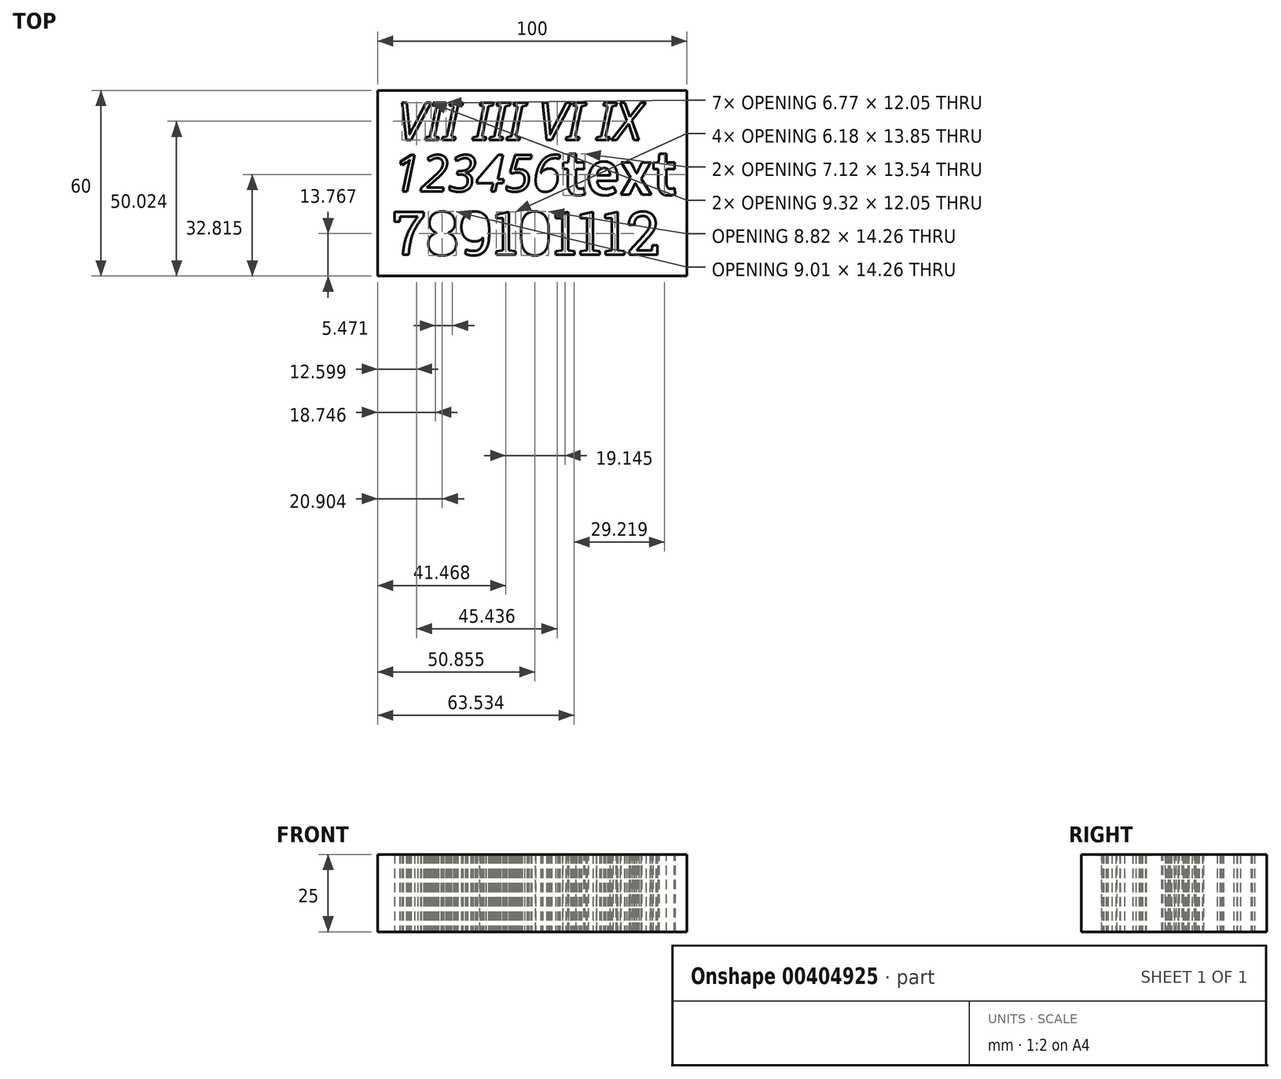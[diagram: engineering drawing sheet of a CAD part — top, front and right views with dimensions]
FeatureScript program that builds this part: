
annotation { "Feature Type Name" : "Feature", "Feature Type Description" : "" }
export const myFeature = defineFeature(function(context is Context, id is Id, definition is map)
    precondition{}
    {
        {
            var Q0;
            Q0=qCreatedBy(makeId("Top.planeOp"),FACE);
            var sketch = newSketch(context, id + "F0", { "sketchPlane" : qUnion([Q0])});
            skText(sketch, "E0", { "text": "VII III VI IX", "fontName": "NotoSans-Italic.ttf"});
            skText(sketch, "E1", { "text": "123456", "fontName": "OpenSans-Italic.ttf"});
            skText(sketch, "E2", { "text": "789101112", "fontName": "RobotoSlab-Regular.ttf"});
            skLineSegment(sketch, "E3.bottom", {"start": v(-47.92, 39.13) * mm, "end": v(52.08, 39.13) * mm});
            skLineSegment(sketch, "E3.top", {"start": v(-47.92, -20.87) * mm, "end": v(52.08, -20.87) * mm});
            skLineSegment(sketch, "E3.left", {"start": v(-47.92, 39.13) * mm, "end": v(-47.92, -20.87) * mm});
            skLineSegment(sketch, "E3.right", {"start": v(52.08, 39.13) * mm, "end": v(52.08, -20.87) * mm});
            const initialGuessF0  = {"E0": [-0.04153, 0.02313, 1, 0, 0.01215], "E1": [-0.04313, 0.0065, 1, 0, 0.01183], "E2": [-0.04313, -0.01403, 1, 0, 0.01403]};
            skSetInitialGuess(sketch, initialGuessF0);
            skSolve(sketch);
        }
        {
            var Q0;
            Q0 = qSketchRegion(id + "F0", true);
            extrude(context, id + "F1", {"entities" : qUnion([Q0]), "depth" : 25 * mm});
        }
        {
            var Q0;
            Q0=makeQuery(id+"F1.opExtrude","CAP_FACE",FACE,{"disambiguationData":[OSD([sQuery(id+"F0.wireOp",EDGE,"E0.sketch_text.stroke-0"),sQuery(id+"F0.wireOp",EDGE,"E0.sketch_text.stroke-1"),sQuery(id+"F0.wireOp",EDGE,"E0.sketch_text.stroke-2"),sQuery(id+"F0.wireOp",EDGE,"E0.sketch_text.stroke-3"),sQuery(id+"F0.wireOp",EDGE,"E0.sketch_text.stroke-4"),sQuery(id+"F0.wireOp",EDGE,"E0.sketch_text.stroke-5"),sQuery(id+"F0.wireOp",EDGE,"E0.sketch_text.stroke-6"),sQuery(id+"F0.wireOp",EDGE,"E0.sketch_text.stroke-7"),sQuery(id+"F0.wireOp",EDGE,"E0.sketch_text.stroke-8"),sQuery(id+"F0.wireOp",EDGE,"E0.sketch_text.stroke-9"),sQuery(id+"F0.wireOp",EDGE,"E0.sketch_text.stroke-10"),sQuery(id+"F0.wireOp",EDGE,"E0.sketch_text.stroke-11"),sQuery(id+"F0.wireOp",EDGE,"E0.sketch_text.stroke-12"),sQuery(id+"F0.wireOp",EDGE,"E0.sketch_text.stroke-13"),sQuery(id+"F0.wireOp",EDGE,"E0.sketch_text.stroke-14"),sQuery(id+"F0.wireOp",EDGE,"E0.sketch_text.stroke-15"),sQuery(id+"F0.wireOp",EDGE,"E0.sketch_text.stroke-16"),sQuery(id+"F0.wireOp",EDGE,"E0.sketch_text.stroke-17"),sQuery(id+"F0.wireOp",EDGE,"E0.sketch_text.stroke-18"),sQuery(id+"F0.wireOp",EDGE,"E0.sketch_text.stroke-19"),sQuery(id+"F0.wireOp",EDGE,"E0.sketch_text.stroke-20"),sQuery(id+"F0.wireOp",EDGE,"E0.sketch_text.stroke-21"),sQuery(id+"F0.wireOp",EDGE,"E0.sketch_text.stroke-22"),sQuery(id+"F0.wireOp",EDGE,"E0.sketch_text.stroke-23"),sQuery(id+"F0.wireOp",EDGE,"E0.sketch_text.stroke-24"),sQuery(id+"F0.wireOp",EDGE,"E0.sketch_text.stroke-25"),sQuery(id+"F0.wireOp",EDGE,"E0.sketch_text.stroke-26"),sQuery(id+"F0.wireOp",EDGE,"E0.sketch_text.stroke-27"),sQuery(id+"F0.wireOp",EDGE,"E0.sketch_text.stroke-28"),sQuery(id+"F0.wireOp",EDGE,"E0.sketch_text.stroke-29"),sQuery(id+"F0.wireOp",EDGE,"E0.sketch_text.stroke-30"),sQuery(id+"F0.wireOp",EDGE,"E0.sketch_text.stroke-31"),sQuery(id+"F0.wireOp",EDGE,"E0.sketch_text.stroke-32"),sQuery(id+"F0.wireOp",EDGE,"E0.sketch_text.stroke-33"),sQuery(id+"F0.wireOp",EDGE,"E0.sketch_text.stroke-34"),sQuery(id+"F0.wireOp",EDGE,"E0.sketch_text.stroke-35"),sQuery(id+"F0.wireOp",EDGE,"E0.sketch_text.stroke-36"),sQuery(id+"F0.wireOp",EDGE,"E0.sketch_text.stroke-37"),sQuery(id+"F0.wireOp",EDGE,"E0.sketch_text.stroke-38"),sQuery(id+"F0.wireOp",EDGE,"E0.sketch_text.stroke-39"),sQuery(id+"F0.wireOp",EDGE,"E0.sketch_text.stroke-40"),sQuery(id+"F0.wireOp",EDGE,"E0.sketch_text.stroke-41"),sQuery(id+"F0.wireOp",EDGE,"E0.sketch_text.stroke-42"),sQuery(id+"F0.wireOp",EDGE,"E0.sketch_text.stroke-43"),sQuery(id+"F0.wireOp",EDGE,"E0.sketch_text.stroke-44"),sQuery(id+"F0.wireOp",EDGE,"E0.sketch_text.stroke-45"),sQuery(id+"F0.wireOp",EDGE,"E0.sketch_text.stroke-46"),sQuery(id+"F0.wireOp",EDGE,"E0.sketch_text.stroke-47"),sQuery(id+"F0.wireOp",EDGE,"E0.sketch_text.stroke-48"),sQuery(id+"F0.wireOp",EDGE,"E0.sketch_text.stroke-49"),sQuery(id+"F0.wireOp",EDGE,"E0.sketch_text.stroke-50"),sQuery(id+"F0.wireOp",EDGE,"E0.sketch_text.stroke-51"),sQuery(id+"F0.wireOp",EDGE,"E0.sketch_text.stroke-52"),sQuery(id+"F0.wireOp",EDGE,"E0.sketch_text.stroke-53"),sQuery(id+"F0.wireOp",EDGE,"E0.sketch_text.stroke-54"),sQuery(id+"F0.wireOp",EDGE,"E0.sketch_text.stroke-55"),sQuery(id+"F0.wireOp",EDGE,"E0.sketch_text.stroke-56"),sQuery(id+"F0.wireOp",EDGE,"E0.sketch_text.stroke-57"),sQuery(id+"F0.wireOp",EDGE,"E0.sketch_text.stroke-58"),sQuery(id+"F0.wireOp",EDGE,"E0.sketch_text.stroke-59"),sQuery(id+"F0.wireOp",EDGE,"E0.sketch_text.stroke-60"),sQuery(id+"F0.wireOp",EDGE,"E0.sketch_text.stroke-61"),sQuery(id+"F0.wireOp",EDGE,"E0.sketch_text.stroke-62"),sQuery(id+"F0.wireOp",EDGE,"E0.sketch_text.stroke-63"),sQuery(id+"F0.wireOp",EDGE,"E0.sketch_text.stroke-64"),sQuery(id+"F0.wireOp",EDGE,"E0.sketch_text.stroke-65"),sQuery(id+"F0.wireOp",EDGE,"E0.sketch_text.stroke-66"),sQuery(id+"F0.wireOp",EDGE,"E0.sketch_text.stroke-67"),sQuery(id+"F0.wireOp",EDGE,"E0.sketch_text.stroke-68"),sQuery(id+"F0.wireOp",EDGE,"E0.sketch_text.stroke-69"),sQuery(id+"F0.wireOp",EDGE,"E0.sketch_text.stroke-70"),sQuery(id+"F0.wireOp",EDGE,"E0.sketch_text.stroke-71"),sQuery(id+"F0.wireOp",EDGE,"E0.sketch_text.stroke-72"),sQuery(id+"F0.wireOp",EDGE,"E0.sketch_text.stroke-73"),sQuery(id+"F0.wireOp",EDGE,"E0.sketch_text.stroke-74"),sQuery(id+"F0.wireOp",EDGE,"E0.sketch_text.stroke-75"),sQuery(id+"F0.wireOp",EDGE,"E0.sketch_text.stroke-76"),sQuery(id+"F0.wireOp",EDGE,"E0.sketch_text.stroke-77"),sQuery(id+"F0.wireOp",EDGE,"E0.sketch_text.stroke-78"),sQuery(id+"F0.wireOp",EDGE,"E0.sketch_text.stroke-79"),sQuery(id+"F0.wireOp",EDGE,"E0.sketch_text.stroke-80"),sQuery(id+"F0.wireOp",EDGE,"E0.sketch_text.stroke-81"),sQuery(id+"F0.wireOp",EDGE,"E0.sketch_text.stroke-82"),sQuery(id+"F0.wireOp",EDGE,"E0.sketch_text.stroke-83"),sQuery(id+"F0.wireOp",EDGE,"E0.sketch_text.stroke-84"),sQuery(id+"F0.wireOp",EDGE,"E0.sketch_text.stroke-85"),sQuery(id+"F0.wireOp",EDGE,"E0.sketch_text.stroke-86"),sQuery(id+"F0.wireOp",EDGE,"E0.sketch_text.stroke-87"),sQuery(id+"F0.wireOp",EDGE,"E0.sketch_text.stroke-88"),sQuery(id+"F0.wireOp",EDGE,"E0.sketch_text.stroke-89"),sQuery(id+"F0.wireOp",EDGE,"E0.sketch_text.stroke-90"),sQuery(id+"F0.wireOp",EDGE,"E0.sketch_text.stroke-91"),sQuery(id+"F0.wireOp",EDGE,"E0.sketch_text.stroke-92"),sQuery(id+"F0.wireOp",EDGE,"E0.sketch_text.stroke-93"),sQuery(id+"F0.wireOp",EDGE,"E0.sketch_text.stroke-94"),sQuery(id+"F0.wireOp",EDGE,"E0.sketch_text.stroke-95"),sQuery(id+"F0.wireOp",EDGE,"E0.sketch_text.stroke-96"),sQuery(id+"F0.wireOp",EDGE,"E0.sketch_text.stroke-97"),sQuery(id+"F0.wireOp",EDGE,"E0.sketch_text.stroke-98"),sQuery(id+"F0.wireOp",EDGE,"E0.sketch_text.stroke-99"),sQuery(id+"F0.wireOp",EDGE,"E0.sketch_text.stroke-100"),sQuery(id+"F0.wireOp",EDGE,"E0.sketch_text.stroke-101"),sQuery(id+"F0.wireOp",EDGE,"E0.sketch_text.stroke-102"),sQuery(id+"F0.wireOp",EDGE,"E0.sketch_text.stroke-103"),sQuery(id+"F0.wireOp",EDGE,"E0.sketch_text.stroke-104"),sQuery(id+"F0.wireOp",EDGE,"E0.sketch_text.stroke-105"),sQuery(id+"F0.wireOp",EDGE,"E0.sketch_text.stroke-106"),sQuery(id+"F0.wireOp",EDGE,"E0.sketch_text.stroke-107"),sQuery(id+"F0.wireOp",EDGE,"E0.sketch_text.stroke-108"),sQuery(id+"F0.wireOp",EDGE,"E0.sketch_text.stroke-109"),sQuery(id+"F0.wireOp",EDGE,"E0.sketch_text.stroke-110"),sQuery(id+"F0.wireOp",EDGE,"E0.sketch_text.stroke-111"),sQuery(id+"F0.wireOp",EDGE,"E0.sketch_text.stroke-112"),sQuery(id+"F0.wireOp",EDGE,"E0.sketch_text.stroke-113"),sQuery(id+"F0.wireOp",EDGE,"E0.sketch_text.stroke-114"),sQuery(id+"F0.wireOp",EDGE,"E0.sketch_text.stroke-115"),sQuery(id+"F0.wireOp",EDGE,"E0.sketch_text.stroke-116"),sQuery(id+"F0.wireOp",EDGE,"E0.sketch_text.stroke-117"),sQuery(id+"F0.wireOp",EDGE,"E1.sketch_text.stroke-0"),sQuery(id+"F0.wireOp",EDGE,"E1.sketch_text.stroke-1"),sQuery(id+"F0.wireOp",EDGE,"E1.sketch_text.stroke-2"),sQuery(id+"F0.wireOp",EDGE,"E1.sketch_text.stroke-3"),sQuery(id+"F0.wireOp",EDGE,"E1.sketch_text.stroke-4"),sQuery(id+"F0.wireOp",EDGE,"E1.sketch_text.stroke-5"),sQuery(id+"F0.wireOp",EDGE,"E1.sketch_text.stroke-6"),sQuery(id+"F0.wireOp",EDGE,"E1.sketch_text.stroke-7"),sQuery(id+"F0.wireOp",EDGE,"E1.sketch_text.stroke-8"),sQuery(id+"F0.wireOp",EDGE,"E1.sketch_text.stroke-9"),sQuery(id+"F0.wireOp",EDGE,"E1.sketch_text.stroke-10"),sQuery(id+"F0.wireOp",EDGE,"E1.sketch_text.stroke-11"),sQuery(id+"F0.wireOp",EDGE,"E1.sketch_text.stroke-12"),sQuery(id+"F0.wireOp",EDGE,"E1.sketch_text.stroke-13"),sQuery(id+"F0.wireOp",EDGE,"E1.sketch_text.stroke-14"),sQuery(id+"F0.wireOp",EDGE,"E1.sketch_text.stroke-15"),sQuery(id+"F0.wireOp",EDGE,"E1.sketch_text.stroke-16"),sQuery(id+"F0.wireOp",EDGE,"E1.sketch_text.stroke-17"),sQuery(id+"F0.wireOp",EDGE,"E1.sketch_text.stroke-18"),sQuery(id+"F0.wireOp",EDGE,"E1.sketch_text.stroke-19"),sQuery(id+"F0.wireOp",EDGE,"E1.sketch_text.stroke-20"),sQuery(id+"F0.wireOp",EDGE,"E1.sketch_text.stroke-21"),sQuery(id+"F0.wireOp",EDGE,"E1.sketch_text.stroke-22"),sQuery(id+"F0.wireOp",EDGE,"E1.sketch_text.stroke-23"),sQuery(id+"F0.wireOp",EDGE,"E1.sketch_text.stroke-24"),sQuery(id+"F0.wireOp",EDGE,"E1.sketch_text.stroke-25"),sQuery(id+"F0.wireOp",EDGE,"E1.sketch_text.stroke-26"),sQuery(id+"F0.wireOp",EDGE,"E1.sketch_text.stroke-27"),sQuery(id+"F0.wireOp",EDGE,"E1.sketch_text.stroke-28"),sQuery(id+"F0.wireOp",EDGE,"E1.sketch_text.stroke-29"),sQuery(id+"F0.wireOp",EDGE,"E1.sketch_text.stroke-30"),sQuery(id+"F0.wireOp",EDGE,"E1.sketch_text.stroke-31"),sQuery(id+"F0.wireOp",EDGE,"E1.sketch_text.stroke-32"),sQuery(id+"F0.wireOp",EDGE,"E1.sketch_text.stroke-33"),sQuery(id+"F0.wireOp",EDGE,"E1.sketch_text.stroke-34"),sQuery(id+"F0.wireOp",EDGE,"E1.sketch_text.stroke-35"),sQuery(id+"F0.wireOp",EDGE,"E1.sketch_text.stroke-36"),sQuery(id+"F0.wireOp",EDGE,"E1.sketch_text.stroke-37"),sQuery(id+"F0.wireOp",EDGE,"E1.sketch_text.stroke-38"),sQuery(id+"F0.wireOp",EDGE,"E1.sketch_text.stroke-39"),sQuery(id+"F0.wireOp",EDGE,"E1.sketch_text.stroke-40"),sQuery(id+"F0.wireOp",EDGE,"E1.sketch_text.stroke-41"),sQuery(id+"F0.wireOp",EDGE,"E1.sketch_text.stroke-42"),sQuery(id+"F0.wireOp",EDGE,"E1.sketch_text.stroke-43"),sQuery(id+"F0.wireOp",EDGE,"E1.sketch_text.stroke-44"),sQuery(id+"F0.wireOp",EDGE,"E1.sketch_text.stroke-45"),sQuery(id+"F0.wireOp",EDGE,"E1.sketch_text.stroke-46"),sQuery(id+"F0.wireOp",EDGE,"E1.sketch_text.stroke-47"),sQuery(id+"F0.wireOp",EDGE,"E1.sketch_text.stroke-48"),sQuery(id+"F0.wireOp",EDGE,"E1.sketch_text.stroke-49"),sQuery(id+"F0.wireOp",EDGE,"E1.sketch_text.stroke-50"),sQuery(id+"F0.wireOp",EDGE,"E1.sketch_text.stroke-51"),sQuery(id+"F0.wireOp",EDGE,"E1.sketch_text.stroke-52"),sQuery(id+"F0.wireOp",EDGE,"E1.sketch_text.stroke-53"),sQuery(id+"F0.wireOp",EDGE,"E1.sketch_text.stroke-54"),sQuery(id+"F0.wireOp",EDGE,"E1.sketch_text.stroke-55"),sQuery(id+"F0.wireOp",EDGE,"E1.sketch_text.stroke-56"),sQuery(id+"F0.wireOp",EDGE,"E1.sketch_text.stroke-57"),sQuery(id+"F0.wireOp",EDGE,"E1.sketch_text.stroke-58"),sQuery(id+"F0.wireOp",EDGE,"E1.sketch_text.stroke-59"),sQuery(id+"F0.wireOp",EDGE,"E1.sketch_text.stroke-60"),sQuery(id+"F0.wireOp",EDGE,"E1.sketch_text.stroke-61"),sQuery(id+"F0.wireOp",EDGE,"E1.sketch_text.stroke-62"),sQuery(id+"F0.wireOp",EDGE,"E1.sketch_text.stroke-63"),sQuery(id+"F0.wireOp",EDGE,"E1.sketch_text.stroke-64"),sQuery(id+"F0.wireOp",EDGE,"E1.sketch_text.stroke-65"),sQuery(id+"F0.wireOp",EDGE,"E1.sketch_text.stroke-66"),sQuery(id+"F0.wireOp",EDGE,"E1.sketch_text.stroke-67"),sQuery(id+"F0.wireOp",EDGE,"E1.sketch_text.stroke-68"),sQuery(id+"F0.wireOp",EDGE,"E1.sketch_text.stroke-69"),sQuery(id+"F0.wireOp",EDGE,"E1.sketch_text.stroke-70"),sQuery(id+"F0.wireOp",EDGE,"E1.sketch_text.stroke-78"),sQuery(id+"F0.wireOp",EDGE,"E1.sketch_text.stroke-79"),sQuery(id+"F0.wireOp",EDGE,"E1.sketch_text.stroke-80"),sQuery(id+"F0.wireOp",EDGE,"E1.sketch_text.stroke-81"),sQuery(id+"F0.wireOp",EDGE,"E1.sketch_text.stroke-82"),sQuery(id+"F0.wireOp",EDGE,"E1.sketch_text.stroke-83"),sQuery(id+"F0.wireOp",EDGE,"E1.sketch_text.stroke-84"),sQuery(id+"F0.wireOp",EDGE,"E1.sketch_text.stroke-85"),sQuery(id+"F0.wireOp",EDGE,"E1.sketch_text.stroke-86"),sQuery(id+"F0.wireOp",EDGE,"E1.sketch_text.stroke-87"),sQuery(id+"F0.wireOp",EDGE,"E1.sketch_text.stroke-88"),sQuery(id+"F0.wireOp",EDGE,"E1.sketch_text.stroke-89"),sQuery(id+"F0.wireOp",EDGE,"E1.sketch_text.stroke-90"),sQuery(id+"F0.wireOp",EDGE,"E1.sketch_text.stroke-91"),sQuery(id+"F0.wireOp",EDGE,"E1.sketch_text.stroke-92"),sQuery(id+"F0.wireOp",EDGE,"E1.sketch_text.stroke-93"),sQuery(id+"F0.wireOp",EDGE,"E1.sketch_text.stroke-94"),sQuery(id+"F0.wireOp",EDGE,"E1.sketch_text.stroke-95"),sQuery(id+"F0.wireOp",EDGE,"E1.sketch_text.stroke-96"),sQuery(id+"F0.wireOp",EDGE,"E1.sketch_text.stroke-97"),sQuery(id+"F0.wireOp",EDGE,"E1.sketch_text.stroke-98"),sQuery(id+"F0.wireOp",EDGE,"E1.sketch_text.stroke-99"),sQuery(id+"F0.wireOp",EDGE,"E1.sketch_text.stroke-100"),sQuery(id+"F0.wireOp",EDGE,"E1.sketch_text.stroke-101"),sQuery(id+"F0.wireOp",EDGE,"E1.sketch_text.stroke-102"),sQuery(id+"F0.wireOp",EDGE,"E1.sketch_text.stroke-103"),sQuery(id+"F0.wireOp",EDGE,"E1.sketch_text.stroke-104"),sQuery(id+"F0.wireOp",EDGE,"E1.sketch_text.stroke-105"),sQuery(id+"F0.wireOp",EDGE,"E1.sketch_text.stroke-106"),sQuery(id+"F0.wireOp",EDGE,"E1.sketch_text.stroke-107"),sQuery(id+"F0.wireOp",EDGE,"E1.sketch_text.stroke-108"),sQuery(id+"F0.wireOp",EDGE,"E1.sketch_text.stroke-109"),sQuery(id+"F0.wireOp",EDGE,"E1.sketch_text.stroke-110"),sQuery(id+"F0.wireOp",EDGE,"E1.sketch_text.stroke-111"),sQuery(id+"F0.wireOp",EDGE,"E1.sketch_text.stroke-112"),sQuery(id+"F0.wireOp",EDGE,"E1.sketch_text.stroke-113"),sQuery(id+"F0.wireOp",EDGE,"E1.sketch_text.stroke-114"),sQuery(id+"F0.wireOp",EDGE,"E1.sketch_text.stroke-115"),sQuery(id+"F0.wireOp",EDGE,"E1.sketch_text.stroke-116"),sQuery(id+"F0.wireOp",EDGE,"E1.sketch_text.stroke-117"),sQuery(id+"F0.wireOp",EDGE,"E2.sketch_text.stroke-0"),sQuery(id+"F0.wireOp",EDGE,"E2.sketch_text.stroke-1"),sQuery(id+"F0.wireOp",EDGE,"E2.sketch_text.stroke-2"),sQuery(id+"F0.wireOp",EDGE,"E2.sketch_text.stroke-3"),sQuery(id+"F0.wireOp",EDGE,"E2.sketch_text.stroke-4"),sQuery(id+"F0.wireOp",EDGE,"E2.sketch_text.stroke-5"),sQuery(id+"F0.wireOp",EDGE,"E2.sketch_text.stroke-6"),sQuery(id+"F0.wireOp",EDGE,"E2.sketch_text.stroke-7"),sQuery(id+"F0.wireOp",EDGE,"E2.sketch_text.stroke-8"),sQuery(id+"F0.wireOp",EDGE,"E2.sketch_text.stroke-9"),sQuery(id+"F0.wireOp",EDGE,"E2.sketch_text.stroke-10"),sQuery(id+"F0.wireOp",EDGE,"E2.sketch_text.stroke-11"),sQuery(id+"F0.wireOp",EDGE,"E2.sketch_text.stroke-12"),sQuery(id+"F0.wireOp",EDGE,"E2.sketch_text.stroke-13"),sQuery(id+"F0.wireOp",EDGE,"E2.sketch_text.stroke-14"),sQuery(id+"F0.wireOp",EDGE,"E2.sketch_text.stroke-15"),sQuery(id+"F0.wireOp",EDGE,"E2.sketch_text.stroke-16"),sQuery(id+"F0.wireOp",EDGE,"E2.sketch_text.stroke-17"),sQuery(id+"F0.wireOp",EDGE,"E2.sketch_text.stroke-18"),sQuery(id+"F0.wireOp",EDGE,"E2.sketch_text.stroke-19"),sQuery(id+"F0.wireOp",EDGE,"E2.sketch_text.stroke-20"),sQuery(id+"F0.wireOp",EDGE,"E2.sketch_text.stroke-21"),sQuery(id+"F0.wireOp",EDGE,"E2.sketch_text.stroke-22"),sQuery(id+"F0.wireOp",EDGE,"E2.sketch_text.stroke-23"),sQuery(id+"F0.wireOp",EDGE,"E2.sketch_text.stroke-24"),sQuery(id+"F0.wireOp",EDGE,"E2.sketch_text.stroke-25"),sQuery(id+"F0.wireOp",EDGE,"E2.sketch_text.stroke-26"),sQuery(id+"F0.wireOp",EDGE,"E2.sketch_text.stroke-27"),sQuery(id+"F0.wireOp",EDGE,"E2.sketch_text.stroke-28"),sQuery(id+"F0.wireOp",EDGE,"E2.sketch_text.stroke-45"),sQuery(id+"F0.wireOp",EDGE,"E2.sketch_text.stroke-46"),sQuery(id+"F0.wireOp",EDGE,"E2.sketch_text.stroke-47"),sQuery(id+"F0.wireOp",EDGE,"E2.sketch_text.stroke-48"),sQuery(id+"F0.wireOp",EDGE,"E2.sketch_text.stroke-49"),sQuery(id+"F0.wireOp",EDGE,"E2.sketch_text.stroke-50"),sQuery(id+"F0.wireOp",EDGE,"E2.sketch_text.stroke-51"),sQuery(id+"F0.wireOp",EDGE,"E2.sketch_text.stroke-52"),sQuery(id+"F0.wireOp",EDGE,"E2.sketch_text.stroke-53"),sQuery(id+"F0.wireOp",EDGE,"E2.sketch_text.stroke-54"),sQuery(id+"F0.wireOp",EDGE,"E2.sketch_text.stroke-55"),sQuery(id+"F0.wireOp",EDGE,"E2.sketch_text.stroke-56"),sQuery(id+"F0.wireOp",EDGE,"E2.sketch_text.stroke-57"),sQuery(id+"F0.wireOp",EDGE,"E2.sketch_text.stroke-58"),sQuery(id+"F0.wireOp",EDGE,"E2.sketch_text.stroke-59"),sQuery(id+"F0.wireOp",EDGE,"E2.sketch_text.stroke-60"),sQuery(id+"F0.wireOp",EDGE,"E2.sketch_text.stroke-61"),sQuery(id+"F0.wireOp",EDGE,"E2.sketch_text.stroke-62"),sQuery(id+"F0.wireOp",EDGE,"E2.sketch_text.stroke-63"),sQuery(id+"F0.wireOp",EDGE,"E2.sketch_text.stroke-73"),sQuery(id+"F0.wireOp",EDGE,"E2.sketch_text.stroke-74"),sQuery(id+"F0.wireOp",EDGE,"E2.sketch_text.stroke-75"),sQuery(id+"F0.wireOp",EDGE,"E2.sketch_text.stroke-76"),sQuery(id+"F0.wireOp",EDGE,"E2.sketch_text.stroke-77"),sQuery(id+"F0.wireOp",EDGE,"E2.sketch_text.stroke-78"),sQuery(id+"F0.wireOp",EDGE,"E2.sketch_text.stroke-79"),sQuery(id+"F0.wireOp",EDGE,"E2.sketch_text.stroke-80"),sQuery(id+"F0.wireOp",EDGE,"E2.sketch_text.stroke-81"),sQuery(id+"F0.wireOp",EDGE,"E2.sketch_text.stroke-82"),sQuery(id+"F0.wireOp",EDGE,"E2.sketch_text.stroke-83"),sQuery(id+"F0.wireOp",EDGE,"E2.sketch_text.stroke-84"),sQuery(id+"F0.wireOp",EDGE,"E2.sketch_text.stroke-85"),sQuery(id+"F0.wireOp",EDGE,"E2.sketch_text.stroke-86"),sQuery(id+"F0.wireOp",EDGE,"E2.sketch_text.stroke-87"),sQuery(id+"F0.wireOp",EDGE,"E2.sketch_text.stroke-88"),sQuery(id+"F0.wireOp",EDGE,"E2.sketch_text.stroke-89"),sQuery(id+"F0.wireOp",EDGE,"E2.sketch_text.stroke-90"),sQuery(id+"F0.wireOp",EDGE,"E2.sketch_text.stroke-91"),sQuery(id+"F0.wireOp",EDGE,"E2.sketch_text.stroke-92"),sQuery(id+"F0.wireOp",EDGE,"E2.sketch_text.stroke-103"),sQuery(id+"F0.wireOp",EDGE,"E2.sketch_text.stroke-104"),sQuery(id+"F0.wireOp",EDGE,"E2.sketch_text.stroke-105"),sQuery(id+"F0.wireOp",EDGE,"E2.sketch_text.stroke-106"),sQuery(id+"F0.wireOp",EDGE,"E2.sketch_text.stroke-107"),sQuery(id+"F0.wireOp",EDGE,"E2.sketch_text.stroke-108"),sQuery(id+"F0.wireOp",EDGE,"E2.sketch_text.stroke-109"),sQuery(id+"F0.wireOp",EDGE,"E2.sketch_text.stroke-110"),sQuery(id+"F0.wireOp",EDGE,"E2.sketch_text.stroke-111"),sQuery(id+"F0.wireOp",EDGE,"E2.sketch_text.stroke-112"),sQuery(id+"F0.wireOp",EDGE,"E2.sketch_text.stroke-113"),sQuery(id+"F0.wireOp",EDGE,"E2.sketch_text.stroke-114"),sQuery(id+"F0.wireOp",EDGE,"E2.sketch_text.stroke-115"),sQuery(id+"F0.wireOp",EDGE,"E2.sketch_text.stroke-116"),sQuery(id+"F0.wireOp",EDGE,"E2.sketch_text.stroke-117"),sQuery(id+"F0.wireOp",EDGE,"E2.sketch_text.stroke-118"),sQuery(id+"F0.wireOp",EDGE,"E2.sketch_text.stroke-119"),sQuery(id+"F0.wireOp",EDGE,"E2.sketch_text.stroke-120"),sQuery(id+"F0.wireOp",EDGE,"E2.sketch_text.stroke-121"),sQuery(id+"F0.wireOp",EDGE,"E2.sketch_text.stroke-122"),sQuery(id+"F0.wireOp",EDGE,"E2.sketch_text.stroke-123"),sQuery(id+"F0.wireOp",EDGE,"E2.sketch_text.stroke-124"),sQuery(id+"F0.wireOp",EDGE,"E2.sketch_text.stroke-125"),sQuery(id+"F0.wireOp",EDGE,"E2.sketch_text.stroke-126"),sQuery(id+"F0.wireOp",EDGE,"E2.sketch_text.stroke-127"),sQuery(id+"F0.wireOp",EDGE,"E2.sketch_text.stroke-128"),sQuery(id+"F0.wireOp",EDGE,"E2.sketch_text.stroke-129"),sQuery(id+"F0.wireOp",EDGE,"E2.sketch_text.stroke-130"),sQuery(id+"F0.wireOp",EDGE,"E2.sketch_text.stroke-131"),sQuery(id+"F0.wireOp",EDGE,"E2.sketch_text.stroke-132"),sQuery(id+"F0.wireOp",EDGE,"E2.sketch_text.stroke-133"),sQuery(id+"F0.wireOp",EDGE,"E2.sketch_text.stroke-134"),sQuery(id+"F0.wireOp",EDGE,"E2.sketch_text.stroke-135"),sQuery(id+"F0.wireOp",EDGE,"E2.sketch_text.stroke-136"),sQuery(id+"F0.wireOp",EDGE,"E2.sketch_text.stroke-137"),sQuery(id+"F0.wireOp",EDGE,"E2.sketch_text.stroke-138"),sQuery(id+"F0.wireOp",EDGE,"E2.sketch_text.stroke-139"),sQuery(id+"F0.wireOp",EDGE,"E2.sketch_text.stroke-140"),sQuery(id+"F0.wireOp",EDGE,"E2.sketch_text.stroke-141"),sQuery(id+"F0.wireOp",EDGE,"E2.sketch_text.stroke-142"),sQuery(id+"F0.wireOp",EDGE,"E2.sketch_text.stroke-143"),sQuery(id+"F0.wireOp",EDGE,"E2.sketch_text.stroke-144"),sQuery(id+"F0.wireOp",EDGE,"E2.sketch_text.stroke-145"),sQuery(id+"F0.wireOp",EDGE,"E2.sketch_text.stroke-146"),sQuery(id+"F0.wireOp",EDGE,"E2.sketch_text.stroke-147"),sQuery(id+"F0.wireOp",EDGE,"E2.sketch_text.stroke-148"),sQuery(id+"F0.wireOp",EDGE,"E2.sketch_text.stroke-149"),sQuery(id+"F0.wireOp",EDGE,"E2.sketch_text.stroke-150"),sQuery(id+"F0.wireOp",EDGE,"E2.sketch_text.stroke-151"),sQuery(id+"F0.wireOp",EDGE,"E2.sketch_text.stroke-152"),sQuery(id+"F0.wireOp",EDGE,"E2.sketch_text.stroke-153"),sQuery(id+"F0.wireOp",EDGE,"E2.sketch_text.stroke-154"),sQuery(id+"F0.wireOp",EDGE,"E2.sketch_text.stroke-155"),sQuery(id+"F0.wireOp",EDGE,"E3.bottom"),sQuery(id+"F0.wireOp",EDGE,"E3.top"),sQuery(id+"F0.wireOp",EDGE,"E3.left"),sQuery(id+"F0.wireOp",EDGE,"E3.right")])],"isStart":false});
            var sketch = newSketch(context, id + "F2", { "sketchPlane" : qUnion([Q0])});
            skText(sketch, "E4", { "text": "text", "fontName": "NotoSansCJKjp-Bold.otf"});
            const initialGuessF2  = {"E4": [0.01166, 0.00544, 1, 0, 0.01346]};
            skSetInitialGuess(sketch, initialGuessF2);
            skSolve(sketch);
        }
        {
            var Q0;
            Q0 = qSketchRegion(id + "F2", true);
            extrude(context, id + "F3", {"entities" : qUnion([Q0]), "operationType" : NewBodyOperationType.REMOVE, "oppositeDirection" : true, "depth" : 25 * mm});
        }
    });
